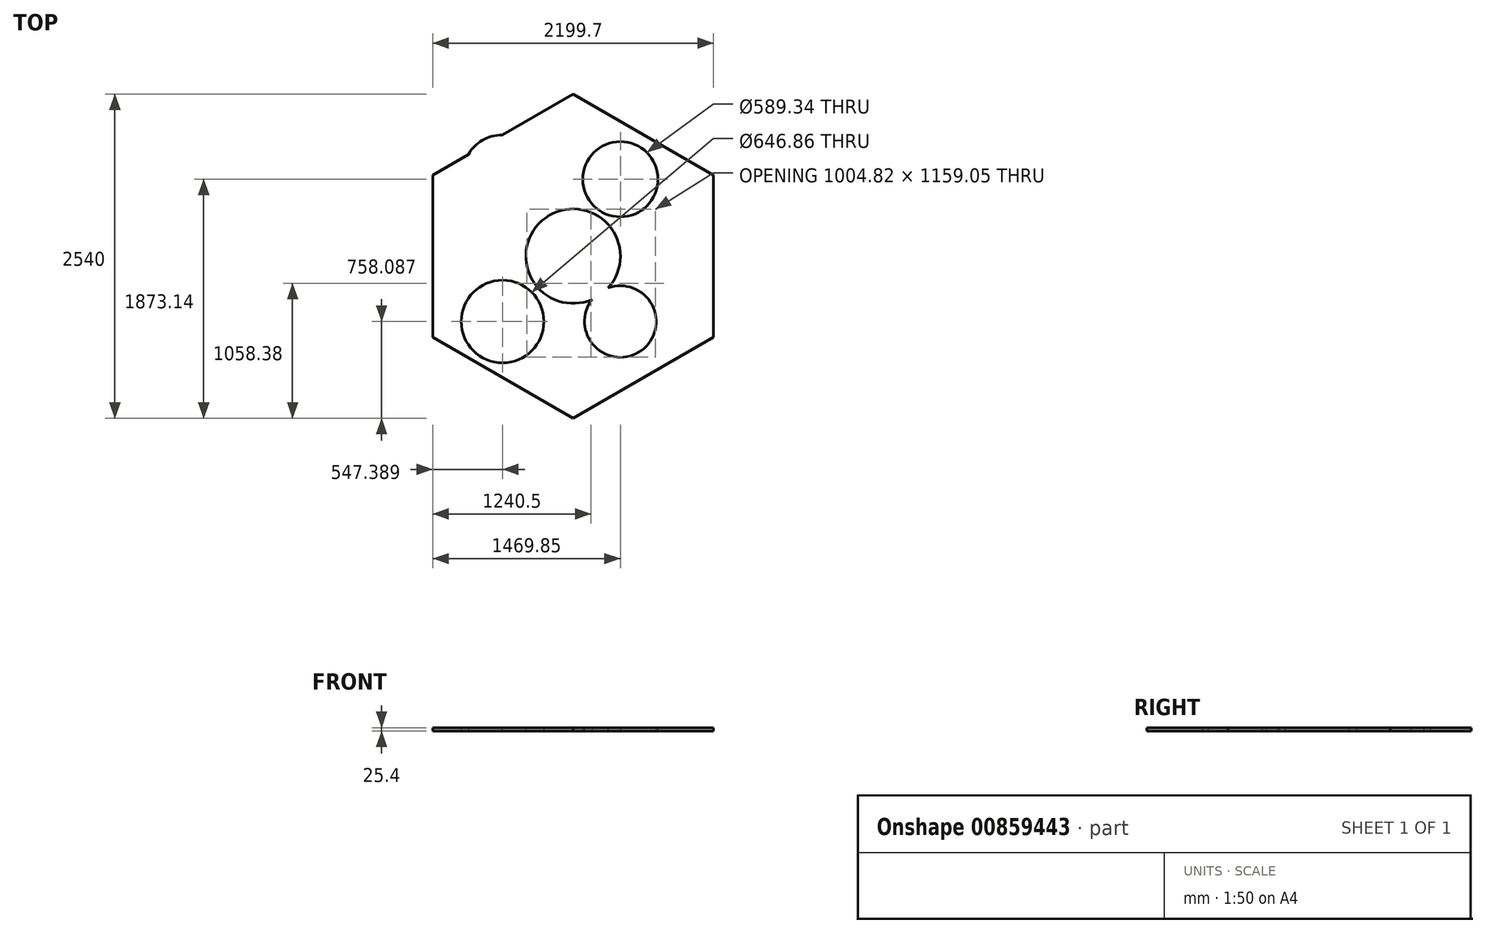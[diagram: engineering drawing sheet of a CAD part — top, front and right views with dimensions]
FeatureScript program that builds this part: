
annotation { "Feature Type Name" : "Feature", "Feature Type Description" : "" }
export const myFeature = defineFeature(function(context is Context, id is Id, definition is map)
    precondition{}
    {
        {
            var Q0;
            Q0=qCreatedBy(makeId("Top.planeOp"),FACE);
            var sketch = newSketch(context, id + "F0", { "sketchPlane" : qUnion([Q0])});
            skCircle(sketch, "E0.cCircle", {"center": v(0, 0) * mm, "radius": 1099.85 * mm, "construction": true});
            skLineSegment(sketch, "E0.0", {"start": v(1099.85, 635) * mm, "end": v(1099.85, -635) * mm});
            skLineSegment(sketch, "E0.1", {"start": v(1099.85, -635) * mm, "end": v(0, -1270) * mm});
            skLineSegment(sketch, "E0.2", {"start": v(0, -1270) * mm, "end": v(-1099.85, -635) * mm});
            skLineSegment(sketch, "E0.3", {"start": v(-1099.85, -635) * mm, "end": v(-1099.85, 635) * mm});
            skLineSegment(sketch, "E0.4", {"start": v(-1099.85, 635) * mm, "end": v(0, 1270) * mm});
            skLineSegment(sketch, "E0.5", {"start": v(0, 1270) * mm, "end": v(1099.85, 635) * mm});
            skPoint(sketch, "E0.0.midPoint", {"position": v(1099.85, 0) * mm});
            skCircle(sketch, "E1", {"center": v(0, 0) * mm, "radius": 370.03 * mm});
            skCircle(sketch, "E2", {"center": v(370, 603.14) * mm, "radius": 294.67 * mm});
            skCircle(sketch, "E3", {"center": v(370, -511.91) * mm, "radius": 280.37 * mm});
            skCircle(sketch, "E4", {"center": v(-552.46, -511.91) * mm, "radius": 323.43 * mm});
            skCircle(sketch, "E5", {"center": v(-562.6, 653.83) * mm, "radius": 294.67 * mm});
            skSolve(sketch);
        }
        {
            var Q0;
            Q0 = qSketchRegion(id + "F0", true);
            extrude(context, id + "F1", {"entities" : qUnion([Q0]), "depth" : 25.4 * mm, "offsetDistance" : 25.4 * mm});
        }
    });
